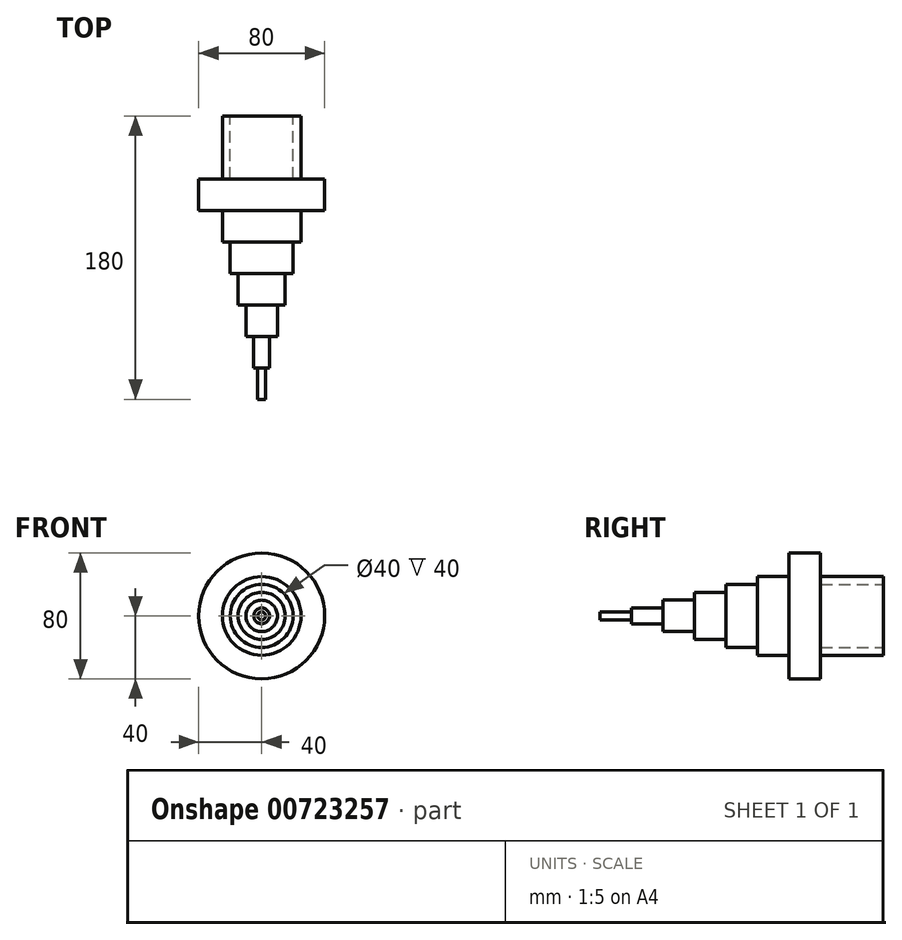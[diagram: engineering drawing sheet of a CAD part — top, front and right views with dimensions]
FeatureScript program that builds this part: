
annotation { "Feature Type Name" : "Feature", "Feature Type Description" : "" }
export const myFeature = defineFeature(function(context is Context, id is Id, definition is map)
    precondition{}
    {
        {
            var Q0;
            Q0=qCreatedBy(makeId("Front.planeOp"),FACE);
            var sketch = newSketch(context, id + "F0", { "sketchPlane" : qUnion([Q0])});
            skCircle(sketch, "E0", {"center": v(0, 0) * mm, "radius": 40 * mm});
            skSolve(sketch);
        }
        {
            var Q0;
            Q0 = qSketchRegion(id + "F0", true);
            extrude(context, id + "F1", {"entities" : qUnion([Q0]), "depth" : 20 * mm, "offsetDistance" : 25.4 * mm});
        }
        {
            var Q0;
            Q0=makeQuery(id+"F1.opExtrude","CAP_FACE",FACE,{"disambiguationData":[OSD([sQuery(id+"F0.wireOp",EDGE,"E0")])],"isStart":false});
            var sketch = newSketch(context, id + "F2", { "sketchPlane" : qUnion([Q0])});
            skCircle(sketch, "E1", {"center": v(0, 0) * mm, "radius": 25 * mm});
            skSolve(sketch);
        }
        {
            var Q0;
            Q0 = qSketchRegion(id + "F2", true);
            extrude(context, id + "F3", {"entities" : qUnion([Q0]), "operationType" : NewBodyOperationType.ADD, "depth" : 20 * mm, "offsetDistance" : 25.4 * mm});
        }
        {
            var Q0;
            Q0=makeQuery(id+"F3.opExtrude","CAP_FACE",FACE,{"disambiguationData":[OSD([sQuery(id+"F2.wireOp",EDGE,"E1")])],"isStart":false});
            var sketch = newSketch(context, id + "F4", { "sketchPlane" : qUnion([Q0])});
            skCircle(sketch, "E2", {"center": v(0, 0) * mm, "radius": 20 * mm});
            skSolve(sketch);
        }
        {
            var Q0;
            Q0 = qSketchRegion(id + "F4", true);
            extrude(context, id + "F5", {"entities" : qUnion([Q0]), "operationType" : NewBodyOperationType.ADD, "depth" : 20 * mm, "offsetDistance" : 25.4 * mm});
        }
        {
            var Q0;
            Q0=makeQuery(id+"F5.opExtrude","CAP_FACE",FACE,{"disambiguationData":[OSD([sQuery(id+"F4.wireOp",EDGE,"E2")])],"isStart":false});
            var sketch = newSketch(context, id + "F6", { "sketchPlane" : qUnion([Q0])});
            skCircle(sketch, "E3", {"center": v(0, 0) * mm, "radius": 15 * mm});
            skSolve(sketch);
        }
        {
            var Q0;
            Q0 = qSketchRegion(id + "F6", true);
            extrude(context, id + "F7", {"entities" : qUnion([Q0]), "operationType" : NewBodyOperationType.ADD, "depth" : 20 * mm, "offsetDistance" : 25.4 * mm});
        }
        {
            var Q0;
            Q0=makeQuery(id+"F7.opExtrude","CAP_FACE",FACE,{"disambiguationData":[OSD([sQuery(id+"F6.wireOp",EDGE,"E3")])],"isStart":false});
            var sketch = newSketch(context, id + "F8", { "sketchPlane" : qUnion([Q0])});
            skCircle(sketch, "E4", {"center": v(0, 0) * mm, "radius": 10 * mm});
            skSolve(sketch);
        }
        {
            var Q0;
            Q0 = qSketchRegion(id + "F8", true);
            extrude(context, id + "F9", {"entities" : qUnion([Q0]), "operationType" : NewBodyOperationType.ADD, "depth" : 20 * mm, "offsetDistance" : 25.4 * mm});
        }
        {
            var Q0;
            Q0=makeQuery(id+"F9.opExtrude","CAP_FACE",FACE,{"disambiguationData":[OSD([sQuery(id+"F8.wireOp",EDGE,"E4")])],"isStart":false});
            var sketch = newSketch(context, id + "F10", { "sketchPlane" : qUnion([Q0])});
            skCircle(sketch, "E5", {"center": v(0, 0) * mm, "radius": 5 * mm});
            skSolve(sketch);
        }
        {
            var Q0;
            Q0 = qSketchRegion(id + "F10", true);
            extrude(context, id + "F11", {"entities" : qUnion([Q0]), "operationType" : NewBodyOperationType.ADD, "depth" : 20 * mm, "offsetDistance" : 25.4 * mm});
        }
        {
            var Q0;
            Q0=makeQuery(id+"F11.opExtrude","CAP_FACE",FACE,{"disambiguationData":[OSD([sQuery(id+"F10.wireOp",EDGE,"E5")])],"isStart":false});
            var sketch = newSketch(context, id + "F12", { "sketchPlane" : qUnion([Q0])});
            skCircle(sketch, "E6", {"center": v(0, 0) * mm, "radius": 2.5 * mm});
            skSolve(sketch);
        }
        {
            var Q0;
            Q0 = qSketchRegion(id + "F12", true);
            extrude(context, id + "F13", {"entities" : qUnion([Q0]), "operationType" : NewBodyOperationType.ADD, "depth" : 20 * mm, "offsetDistance" : 25.4 * mm});
        }
        {
            var Q0;
            Q0=makeQuery(id+"F1.opExtrude","CAP_FACE",FACE,{"disambiguationData":[OSD([sQuery(id+"F0.wireOp",EDGE,"E0")])],"isStart":true});
            var sketch = newSketch(context, id + "F14", { "sketchPlane" : qUnion([Q0])});
            skCircle(sketch, "E7", {"center": v(0, 0) * mm, "radius": 25 * mm});
            skSolve(sketch);
        }
        {
            var Q0;
            Q0 = qSketchRegion(id + "F14", true);
            extrude(context, id + "F15", {"entities" : qUnion([Q0]), "operationType" : NewBodyOperationType.ADD, "depth" : 40 * mm, "offsetDistance" : 25.4 * mm});
        }
        {
            var Q0;
            Q0=makeQuery(id+"F15.opExtrude","CAP_FACE",FACE,{"disambiguationData":[OSD([sQuery(id+"F14.wireOp",EDGE,"E7")])],"isStart":false});
            var sketch = newSketch(context, id + "F16", { "sketchPlane" : qUnion([Q0])});
            skCircle(sketch, "E8", {"center": v(0, 0) * mm, "radius": 20 * mm});
            skSolve(sketch);
        }
        {
            var Q0;
            Q0=makeQuery(id+"F16.imprint","IMPRINT",FACE,{"disambiguationData":[TD([[makeQuery(id+"F16.imprint","IMPRINT",EDGE,{"derivedFrom":sQuery(id+"F16.wireOp",EDGE,"E8")}),1.0]])]});
            extrude(context, id + "F17", {"entities" : qUnion([Q0]), "operationType" : NewBodyOperationType.REMOVE, "oppositeDirection" : true, "depth" : 40 * mm, "offsetDistance" : 25.4 * mm});
        }
    });
